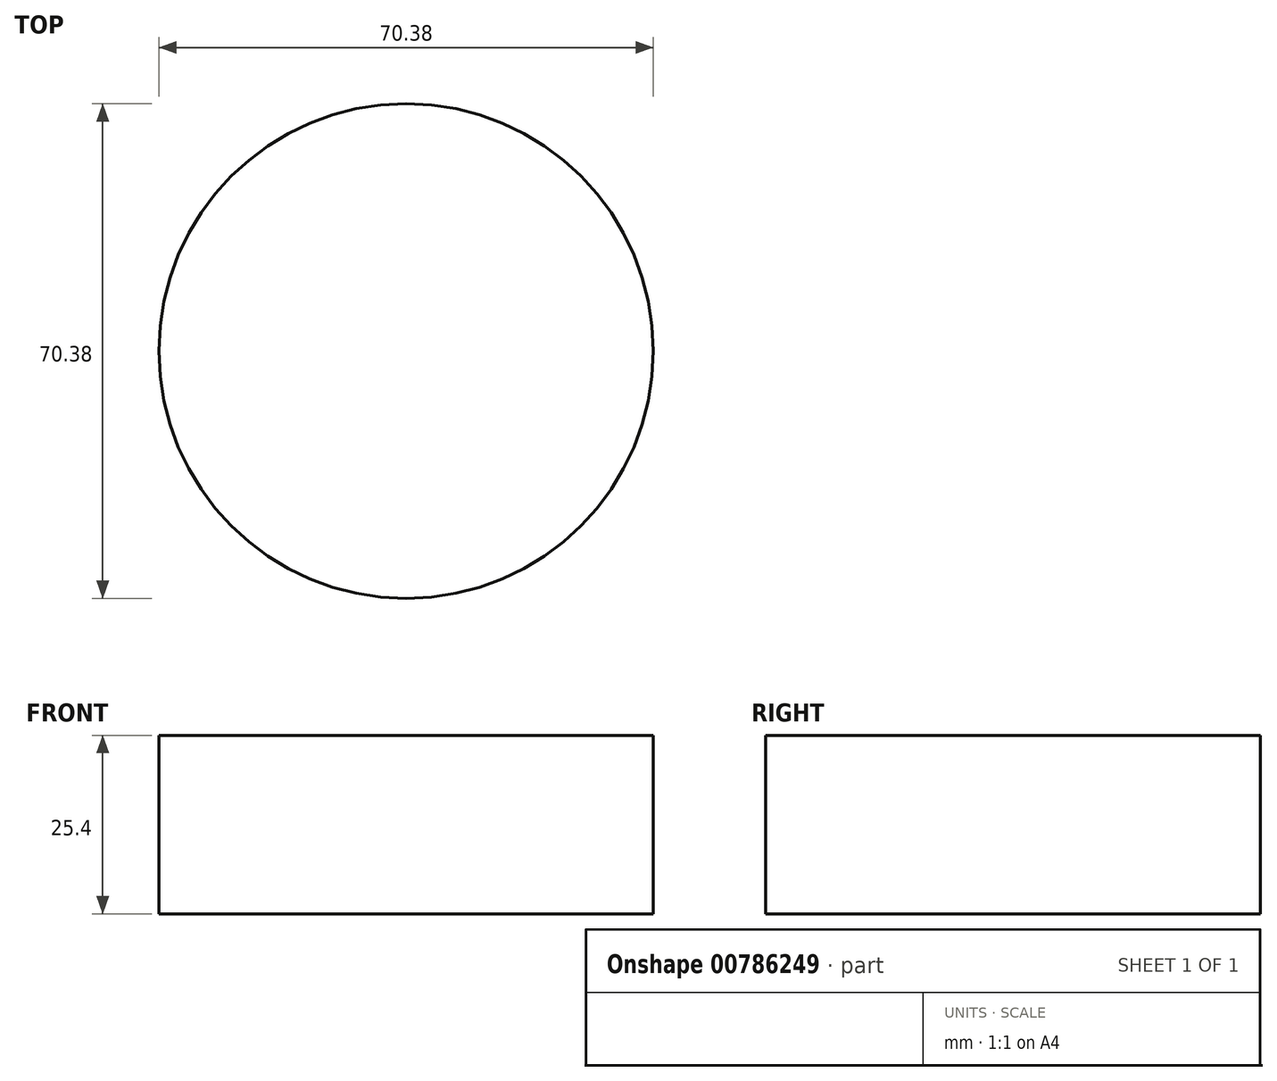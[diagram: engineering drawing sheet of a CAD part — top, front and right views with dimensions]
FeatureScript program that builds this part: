
annotation { "Feature Type Name" : "Feature", "Feature Type Description" : "" }
export const myFeature = defineFeature(function(context is Context, id is Id, definition is map)
    precondition{}
    {
        {
            var Q0;
            Q0=qCreatedBy(makeId("Top.planeOp"),FACE);
            var sketch = newSketch(context, id + "F0", { "sketchPlane" : qUnion([Q0])});
            skCircle(sketch, "E0", {"center": v(0, 0) * mm, "radius": 35.2 * mm});
            skSolve(sketch);
        }
        {
            var Q0;
            Q0 = qSketchRegion(id + "F0", true);
            extrude(context, id + "F1", {"entities" : qUnion([Q0]), "depth" : 25.4 * mm, "offsetDistance" : 25.4 * mm});
        }
    });
